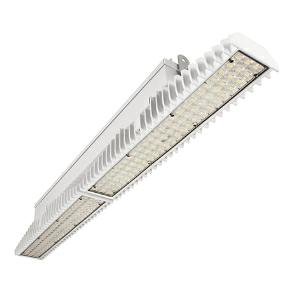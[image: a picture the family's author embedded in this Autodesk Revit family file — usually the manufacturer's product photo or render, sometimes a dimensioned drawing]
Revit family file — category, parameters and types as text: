
# Revit family: 3f_filippi_-_3f_lem_ampio_3f_filippi_-_59161_a0811_-_3f_lem_1_1_led_100-865_cr_ampio___vt_9498
name_source: partatom
category: Lighting Fixtures
units: mm (PartAtom-declared; Revit-internal decimal feet)

## family parameters
Cut with Voids When Loaded = No
Host = Face
Light Source = No
Part Type = Normal
Room Calculation Point = No
Round Connector Dimension = Use Diameter
Shared = No

## types (1)
- 3F Filippi - 3F LEM Ampio (1 x LED, 15821 lm, 109 W, 6500 K)
    Apparent Load = 109 VA
    Approval mark = CE
    CIE Flux Codes = 60 92 99 100 100
    Color Rendering = 80
    Color Temperature = 6500 K
    Control Gear = Electronic ballast
    Default Elevation = 1800 mm
    Description = Industrial luminaire with high light output and high luminous efficiency designed with the most innovative technologies for environments with temperature up to 55°C.

ILLUMINOTECHNICAL
Luminous efficiency 100% (DLOR 99%, ULOR 1%).
Initial luminous flux of the luminaire 15821 lm.
Direct symmetric wide distribution: the illuminated area has a rectangular shape.
Installation Interdistance Transv.D = 1.58 x hu - Long.D = 1.45 x hu.
Tabular UGR (CIE 117 - 4H-8H; S=0.25H; 70/50/20): RUG 25.9 - 26.8.
Beam angle: 93° - 99°.
Luminous efficacy 145 lm/W.
Lifetime (L93/B10): 30000 h. (tq+25°C)
Lifetime (L90/B10): 50000 h. (tq+25°C)
Lifetime (L85/B10): 80000 h. (tq+25°C)
Lifetime (L80/B10): 100000 h. (tq+25°C)
Lifetime (L85/B10): 50000 h. (tq+55°C)
Sudden decreased luminous flux after 50000 hours: 0% (C0).
Photobiological safety in compliance with IEC/TR 62778: RG0 risk exempt, (IEC 62471).
In compliance with IEC/EN 62722-2-1 - IEC/EN 62717 standards.

SOURCE
2 Mid-Power linear LED modules 50W/865.
Energy efficiency class (UE 2019/2020 - UE 2019/2015): C.
CIE 13.3 Colour rendering index: CRI >80 (R9 <50%).
IES TM-30 Fidelity Index: Rf = 84 Rg = 95.
CCT nominal colour temperature 6500 K.
Colour initial tolerance (MacAdam): SDCM 3.

MECHANICAL
Passive modular heatsinks in die-casted aluminium, painted in white colour.
To optimize the thermal management of the LED module, the heatsinks are oversized and provided with self-cleaning of cooling fins.
Wiring body in aluminium and galvanised steel anchored solidly to the sinks and thermally separated.
3F Lens lenses with high luminous efficiency, transparent methacrylate (PMMA), fixed to the LED modules.
Fixing brackets in stainless steel.
Luminaire with limited surface temperature. - D - (EN 60598-2-24)
Dimensions: 1099x115 mm, height 154 mm. Weight 11.464 kg.
IP65 protection degree.
Mechanical strength to impacts IK06 (1 joule).
Glow-wire test resistance 650°C.

ELECTRICAL
Halogen Free electronic wiring 230V-50/60Hz, power factor 0.97, THD <25%, constant output current, class I, 1 driver.
Power of the luminaire 109 W.
ENEC - CE.
SAFE FLICKER: PstLM=<1 and SVM=<0.4 (IEC TR 61547-1 and IEC TR 63158), to ensure a more comfortable and safe light.
Luminaire compliant with EN 60598-2-22 for power supply from a centralised emergency system CPSS (Central Power Supply System), not incorporated in the luminaire - high risk areas excluded. The default power and flux are 100% in AC and 100% in DC.
Ambient temperature from -30°C to +55°C.
Temperature class T6 max 85°C.
Quick connection via M20 3P connector with 9-13 mm tightening range.
Power unit positioned on a separate compartment by the LED module to ensure optimum temperatures of cabling components, to be inspectable and maintainable.
Relative humidity UR: <85%.

INSTALLATION
Ceiling / Suspended / Wall.
All accessories dedicated to this product are available on the Catalog and on our website www.3F-Filippi.com.

ACCESSORIES
A0811 - VT transparent glass, tempered, not flammable, with sealing gasket.
One required for each light module. The pack contains 10 pieces.

APPLICATIONS
In commercial environments, exhibition and industrial areas, stores, open areas.
Applications with high ambient temperature up to 55°C.
Environments in which it is necessary a total protection against falling fragments (eg environments with foodstuffs or machines with moving parts or with extreme temperature changes), use luminaires with polycarbonate lenses.

WARNING
Fixture not suitable for cold stores with an ambient temperature <0°C and/or relative humidity >85%.
Luminaire designed for disposal/recycling at end-of-life.
Replaceable (LED only) light source by a professional. Replaceable control gear by a professional.
    Height = 154 mm
    Lamp = 1 x LED
    Lamp Light Flux = 15821 lm
    Lamp Power = 109 W
    Lamp count = 1
    Length = 1099 mm
    Lifetime = 50000 h
    Luminous efficacy = 145 lm/W
    Manufacturer = 3F Filippi
    ModVariant = No
    Model = 3F Filippi - 59161+A0811 - 3F LEM 1+1 LED 100-865 CR AMPIO + VT
    Mounting Place = Ceiling
    Mounting Type = Pendant
    Number of Poles = 1
    OnlyDefault = Yes
    Power Factor = 1
    Product Name = 3F Filippi - 3F LEM Ampio
    Product group = pendant luminaire
    ProductGroupID = 9
    Protection Class = Protection class I
    Protection Degree = IP 65
    RLX_Detail_Level = 1
    RLX_Emergency_Light_Flux = 0 lm
    RLX_Emergency_Type = 0
    RLX_Emergency_Type_DB = No
    RlxData = <blob elided: 98297 chars, md5=11bfc2e8>
    Socket = socket
    Standby Power = 0 W
    System Light Flux = 15821 lm
    System Power = 109 W
    Type Comments = Product without accessories
    Type Image = 3f_filippi_-_lem_11__a0811.jpg
    URL = http://relux.com
    VarID = ---
    Voltage = 0 V
    Weight = 0.00 kg
    Width = 115 mm

## geometry (parser evidence)
native form markers: Blend x4, Sweep x11
no freeform markers — native parametric forms only
